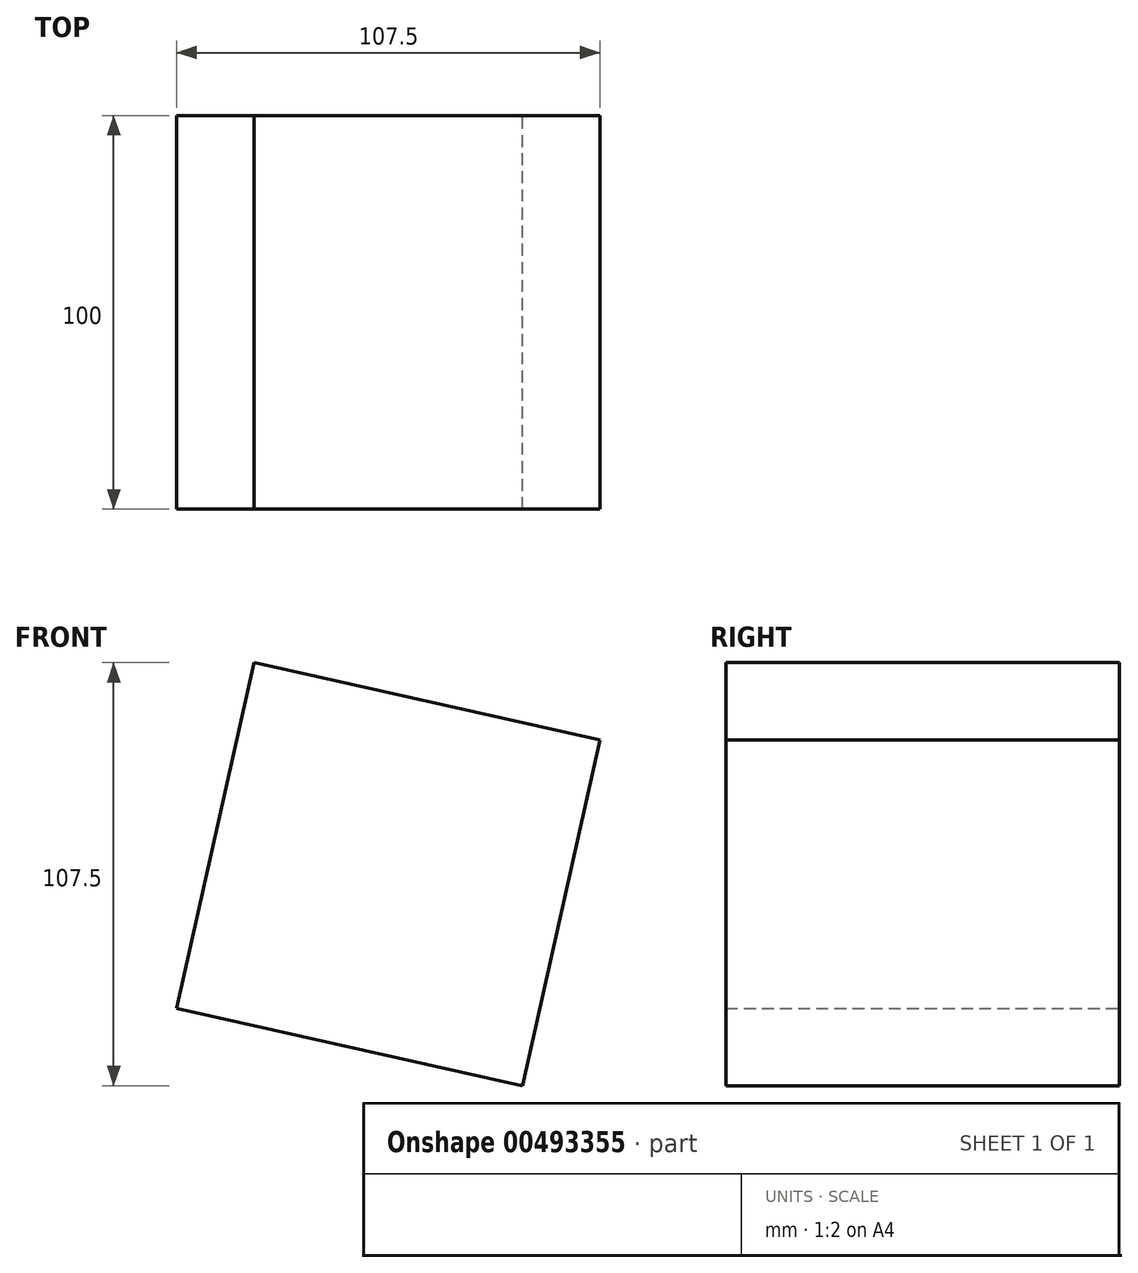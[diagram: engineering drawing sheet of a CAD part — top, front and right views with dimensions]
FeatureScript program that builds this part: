
annotation { "Feature Type Name" : "Feature", "Feature Type Description" : "" }
export const myFeature = defineFeature(function(context is Context, id is Id, definition is map)
    precondition{}
    {
        {
            var Q0;
            Q0=qCreatedBy(makeId("Front.planeOp"),FACE);
            var sketch = newSketch(context, id + "F0", { "sketchPlane" : qUnion([Q0])});
            skCircle(sketch, "E0.cCircle", {"center": v(0, 0) * mm, "radius": 63.64 * mm, "construction": true});
            skLineSegment(sketch, "E0.0", {"start": v(-34.07, 53.75) * mm, "end": v(53.75, 34.07) * mm});
            skLineSegment(sketch, "E0.1", {"start": v(53.75, 34.07) * mm, "end": v(34.07, -53.75) * mm});
            skLineSegment(sketch, "E0.2", {"start": v(34.07, -53.75) * mm, "end": v(-53.75, -34.07) * mm});
            skLineSegment(sketch, "E0.3", {"start": v(-53.75, -34.07) * mm, "end": v(-34.07, 53.75) * mm});
            skSolve(sketch);
        }
        {
            var Q0;
            Q0=makeQuery(id+"F0.imprint","IMPRINT",FACE,{"disambiguationData":[TD([[makeQuery(id+"F0.imprint","IMPRINT",EDGE,{"derivedFrom":sQuery(id+"F0.wireOp",EDGE,"E0.0")}),-1.0]])]});
            extrude(context, id + "F1", {"entities" : qUnion([Q0]), "endBound" : BoundingType.SYMMETRIC, "depth" : 100 * mm});
        }
    });
